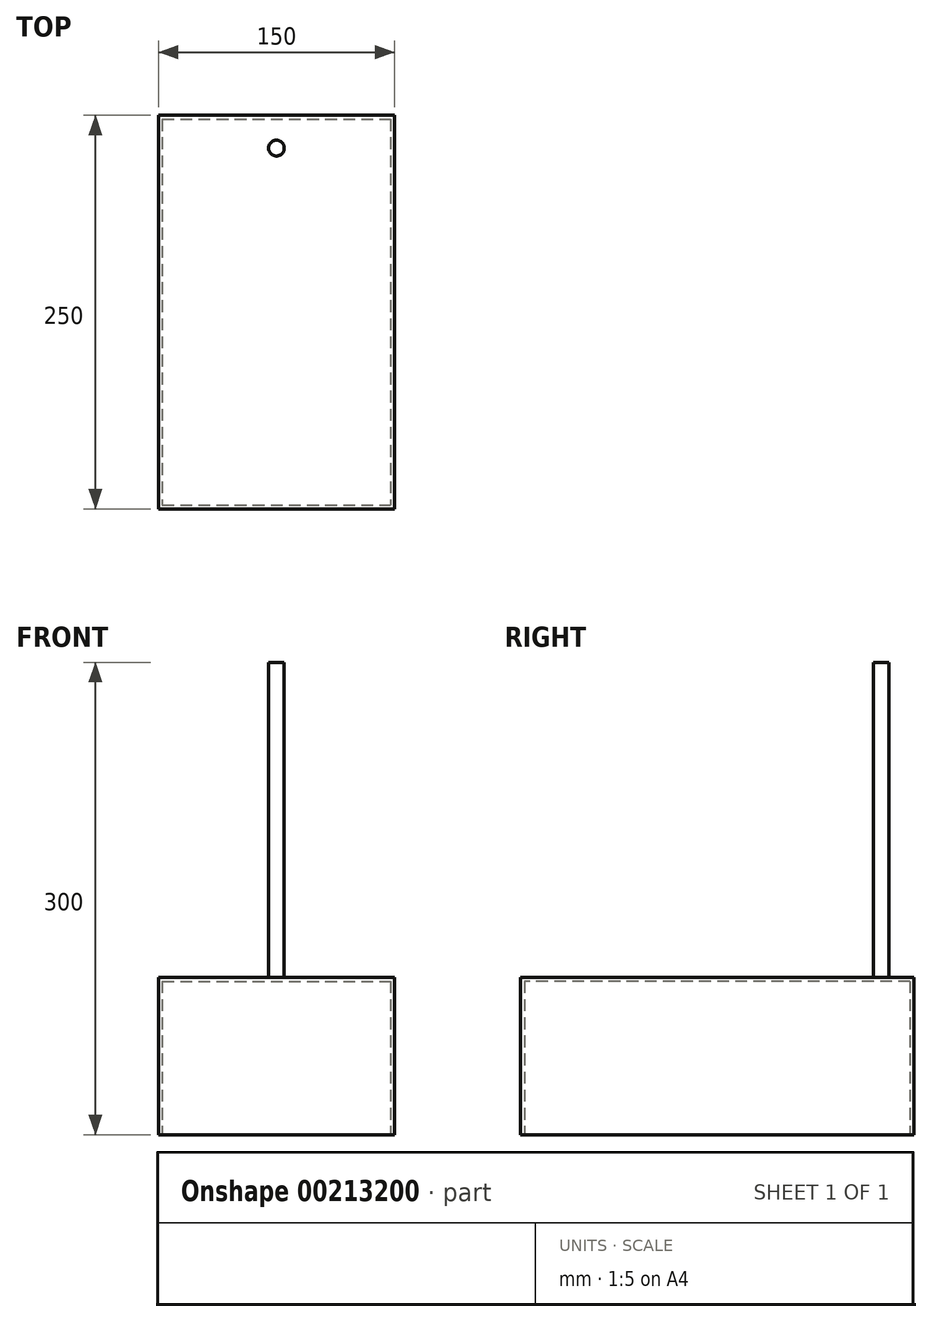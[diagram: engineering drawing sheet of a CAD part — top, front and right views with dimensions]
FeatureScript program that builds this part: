
annotation { "Feature Type Name" : "Feature", "Feature Type Description" : "" }
export const myFeature = defineFeature(function(context is Context, id is Id, definition is map)
    precondition{}
    {
        {
            var Q0;
            Q0=qCreatedBy(makeId("Top.planeOp"),FACE);
            var sketch = newSketch(context, id + "F0", { "sketchPlane" : qUnion([Q0])});
            skLineSegment(sketch, "E0.bottom", {"start": v(-75, 0) * mm, "end": v(75, 0) * mm});
            skLineSegment(sketch, "E0.top", {"start": v(-75, -250) * mm, "end": v(75, -250) * mm});
            skLineSegment(sketch, "E0.left", {"start": v(-75, 0) * mm, "end": v(-75, -250) * mm});
            skLineSegment(sketch, "E0.right", {"start": v(75, 0) * mm, "end": v(75, -250) * mm});
            skSolve(sketch);
        }
        {
            var Q0;
            Q0=makeQuery(id+"F0.imprint","IMPRINT",FACE,{"disambiguationData":[TD([[makeQuery(id+"F0.imprint","IMPRINT",EDGE,{"derivedFrom":sQuery(id+"F0.wireOp",EDGE,"E0.bottom")}),-1.0]])]});
            extrude(context, id + "F1", {"entities" : qUnion([Q0]), "depth" : 100 * mm});
        }
        {
            var Q0;
            Q0=makeQuery(id+"F1.opExtrude","CAP_FACE",FACE,{"disambiguationData":[OSD([sQuery(id+"F0.wireOp",EDGE,"E0.bottom"),sQuery(id+"F0.wireOp",EDGE,"E0.top"),sQuery(id+"F0.wireOp",EDGE,"E0.left"),sQuery(id+"F0.wireOp",EDGE,"E0.right")])],"isStart":true});
            shell(context, id + "F2", {"entities" : qUnion([Q0]), "thickness" : 2.5 * mm});
        }
        {
            var Q0;
            Q0=makeQuery(id+"F1.opExtrude","CAP_FACE",FACE,{"disambiguationData":[OSD([sQuery(id+"F0.wireOp",EDGE,"E0.bottom"),sQuery(id+"F0.wireOp",EDGE,"E0.top"),sQuery(id+"F0.wireOp",EDGE,"E0.left"),sQuery(id+"F0.wireOp",EDGE,"E0.right")])],"isStart":false});
            var sketch = newSketch(context, id + "F3", { "sketchPlane" : qUnion([Q0])});
            skCircle(sketch, "E1", {"center": v(0, -20.85) * mm, "radius": 5 * mm});
            skSolve(sketch);
        }
        {
            var Q0;
            Q0=makeQuery(id+"F3.imprint","IMPRINT",FACE,{"disambiguationData":[TD([[makeQuery(id+"F3.imprint","IMPRINT",EDGE,{"derivedFrom":sQuery(id+"F3.wireOp",EDGE,"E1")}),1.0]])]});
            extrude(context, id + "F4", {"entities" : qUnion([Q0]), "operationType" : NewBodyOperationType.ADD, "depth" : 200 * mm});
        }
    });
